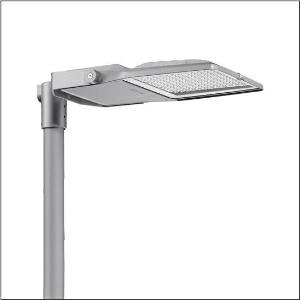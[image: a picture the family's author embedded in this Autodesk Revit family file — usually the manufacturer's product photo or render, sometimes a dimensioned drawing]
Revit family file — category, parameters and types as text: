
# Revit family: floodlight_fl_21_iq_midi___pl61_5xa7781e4c3a_96c8
name_source: partatom
category: Lighting Fixtures
units: mm (PartAtom-declared; Revit-internal decimal feet)

## family parameters
Cut with Voids When Loaded = No
Host = Face
Light Source = No
Part Type = Normal
Room Calculation Point = No
Round Connector Dimension = Use Diameter
Shared = No

## types (1)
- --- (1 x LED, 27490 lm, 208.1 W, 4000K)
    Apparent Load = 208 VA
    CIE Flux Codes = 33 65 98 100 100
    Color Rendering = 70
    Color Temperature = 4000K
    Default Elevation = 1800 mm
    Description = Floodlight FL 21 iQ midi, floodlight, primary light control with lens, of PMMA, primary optical cover: protective disc, of toughened safety glass, transparent, light distribution: PL61, light emission: direct distribution, installation type: surface-mounted, lamps: LED, High Power LED, rated values: 27.490lm | 208,1W | 132,1lm/W (begin service life); end service life: 27.490lm | 227,1W; at 50% lumin. flux: 13.745lm | 90,3W | 152,2lm/W, colour temperature: 4000K, colour rendering: CRI > 70, light colour: 740, light setting 1 begin service life: 100% | 27.490lm | 208,1W | 132,1lm/W | 4.000K, light setting 1 end service life: 227,1W, further light settings possible, control: optimised constant luminous flux control (CLO 2.0), Desk-Remote (wireless, voltage-free reading and setting of iQ features in the workshop via application-optimized NFC function/RFID function), Light-Fading, Smart-Wire, Night-Set, Lumen-Switch, Temp-Guard, Auto-Match, pre-setting: linear dimming characteristic, with terminal, 6-pole, mains connection: 220..240V, AC, 50/60Hz, luminaire housing, of diecast aluminium, powder-coated, SITECO metallic grey (DB 702S), corrosivity category C5 mid according to DIN EN ISO 12944suitable for swimming poolschlorine-resistant, sealing non-destructively replaceable, please order mast flange separately, mast bracket, of steel, galvanised, powder-coated, SITECO metallic grey (DB 702S), protection rating (complete): IP66, insulation class (complete): insulation class II (safety insulation), certification: CE, ENEC, VDE, protection symbol: D, impact resistance: IK08, permissible operating ambient temperature: -40..+40°C, permissible operating ambient temperature for outdoor applications: -40..+50°C, standard: DIN EN 12944, LABS conformity tested according to VDMA 24364:2018-05, packaging unit: 1 piece

Light Distribution: PL61
    Height = 76 mm
    Lamp = 1 x LED
    Lamp Light Flux = 27490 lm
    Lamp Power = 208.1 W
    Lamp count = 1
    Length = 657 mm
    Luminous efficacy = 132 lm/W
    Manufacturer = Siteco
    ModVariant = No
    Model = 5XA7781E4C3A
    Mounting Place = Pole
    Mounting Type = Pole annexe
    Number of Poles = 1
    OnlyDefault = Yes
    Power Factor = 1
    Product Name = Floodlight FL 21 iQ midi | PL61
    Product group = floodlight | pylon annexe
    ProductGroupID = 6201
    Protection Class = Protection class II
    Protection Degree = IP 66
    RLX_Detail_Level = 1
    RLX_Emergency_Light_Flux = 0 lm
    RLX_Emergency_Type = 0
    RLX_Emergency_Type_DB = No
    RlxData = <blob elided: 153965 chars, md5=f131c956>
    Socket = socket
    Standby Power = 0 W
    System Light Flux = 27490 lm
    System Power = 208 W
    Type Comments = factory setting: luminous flux: 100 % | dim-lin: 254 | 710 mA
    Type Image = l_1007123.jpg
    URL = http://relux.com
    VarID = @adj_110363
    Voltage = 0 V
    Weight = 0.00 kg
    Width = 442 mm

## geometry (parser evidence)
native form markers: Blend x4, Sweep x12
no freeform markers — native parametric forms only
